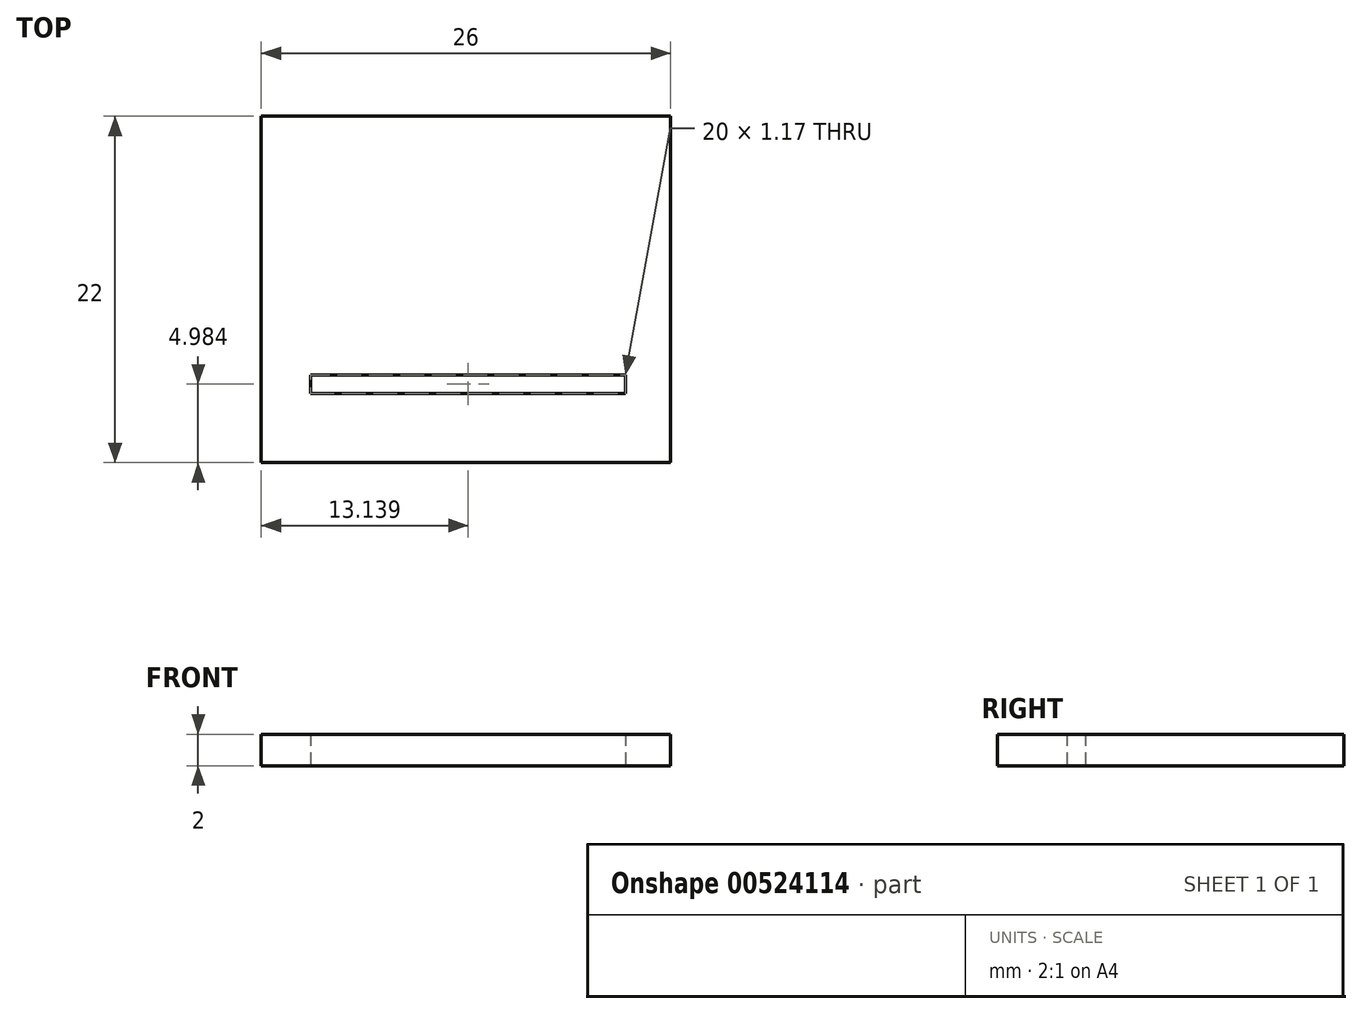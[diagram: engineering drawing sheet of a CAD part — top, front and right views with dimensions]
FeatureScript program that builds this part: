
annotation { "Feature Type Name" : "Feature", "Feature Type Description" : "" }
export const myFeature = defineFeature(function(context is Context, id is Id, definition is map)
    precondition{}
    {
        {
            var Q0;
            Q0=qCreatedBy(makeId("Top.planeOp"),FACE);
            var sketch = newSketch(context, id + "F0", { "sketchPlane" : qUnion([Q0])});
            skLineSegment(sketch, "E0.top", {"start": v(13, 8.5) * mm, "end": v(-13, 8.5) * mm});
            skLineSegment(sketch, "E0.left", {"start": v(13, -8.5) * mm, "end": v(13, 8.5) * mm});
            skLineSegment(sketch, "E0.right", {"start": v(-13, -8.5) * mm, "end": v(-13, 8.5) * mm});
            skPoint(sketch, "E0.middle", {"position": v(0, 0) * mm});
            skLineSegment(sketch, "E1", {"start": v(-13, -8.5) * mm, "end": v(-13, -13.5) * mm});
            skLineSegment(sketch, "E2", {"start": v(13, -8.5) * mm, "end": v(13, -13.5) * mm});
            skLineSegment(sketch, "E3", {"start": v(-13, -13.5) * mm, "end": v(13, -13.5) * mm});
            skLineSegment(sketch, "E4", {"start": v(10.14, -9.1) * mm, "end": v(-9.86, -9.1) * mm});
            skLineSegment(sketch, "E5", {"start": v(10.14, -9.1) * mm, "end": v(10.14, -7.93) * mm});
            skLineSegment(sketch, "E6", {"start": v(-9.86, -9.1) * mm, "end": v(-9.86, -7.93) * mm});
            skLineSegment(sketch, "E7", {"start": v(-9.86, -7.93) * mm, "end": v(10.14, -7.93) * mm});
            skLineSegment(sketch, "E8", {"start": v(-1410.53, -9.08) * mm, "end": v(-1410.53, -13.5) * mm});
            skLineSegment(sketch, "E9", {"start": v(6.25, -9.1) * mm, "end": v(6.25, -13.5) * mm});
            skSolve(sketch);
        }
        {
            var Q0;
            Q0=makeQuery(id+"F0.imprint","IMPRINT",FACE,{"disambiguationData":[TD([[makeQuery(id+"F0.imprint","IMPRINT",EDGE,{"derivedFrom":sQuery(id+"F0.wireOp",EDGE,"E0.top")}),1.0]])]});
            extrude(context, id + "F1", {"entities" : qUnion([Q0]), "depth" : 2 * mm, "offsetDistance" : 25 * mm});
        }
    });
